# Revit family: Inbox Booths_Medium Booth
name_source: partatom
category: Furniture
units: mm (PartAtom-declared; Revit-internal decimal feet)

## family parameters
Always vertical = Yes
Cut with Voids When Loaded = No
Enable Cutting in Views = No
OmniClass Number = 23.40.20.00
OmniClass Title = General Furniture and Specialties
Render Appearance Source = Family Geometry
Room Calculation Point = No
Shared = No
Work Plane-Based = No

## types (1)
- Inbox Booths_Medium Booth
    AREA (DO NOT EDIT) = 1929 mm
    BB_Door Swing = Yes
    BB_Exterior Shell = Default
    BB_Floor Carpet = Default
    BB_Glass = Glass
    BB_Glass Edge (non-editable finish) = Default
    BB_Hardware (non-editable finish) = Default
    BB_Light Source = Default Light Source
    BB_Pet Panel = Default
    BB_Set Out Lines = Yes
    BIM Content Publish Date = 26.4.2024
    BIM Content Publish Revit Version = Revit 2024.1
    DEPTH (DO NOT EDIT) = 1286 mm  [stored 4.21916 ft]
    Description = Medium portable privacy booth offers individual users a confidential space for phone calls or private meetings in any environment.
portable privacy booth offers individual users a confidential space for phone calls or private meetings in any environment.
portable privacy booth offers individual users a confidential space for phone calls or private meetings in any environment.
    HEIGHT (DO NOT EDIT) = 2300 mm
    Manufacturer = Inbox Booths
    Model = Medium Booth
    OwnedBy = Inbox Booths
    Product Category = Loose Furniture
    Product Specific URL (Manufacturer) = https://inboxbooths.com
    Type Comments = Medium Booth
    URL = https://inboxbooths.com
    WEIGHT (DO NOT EDIT) = 387 kg
    WIDTH (DO NOT EDIT) = 1500 mm

note: [stored X ft] marks values corroborated as IEEE doubles in the binary element streams (Revit-internal decimal feet)

## geometry (parser evidence)
native form markers: Sweep x2
no freeform markers — native parametric forms only
